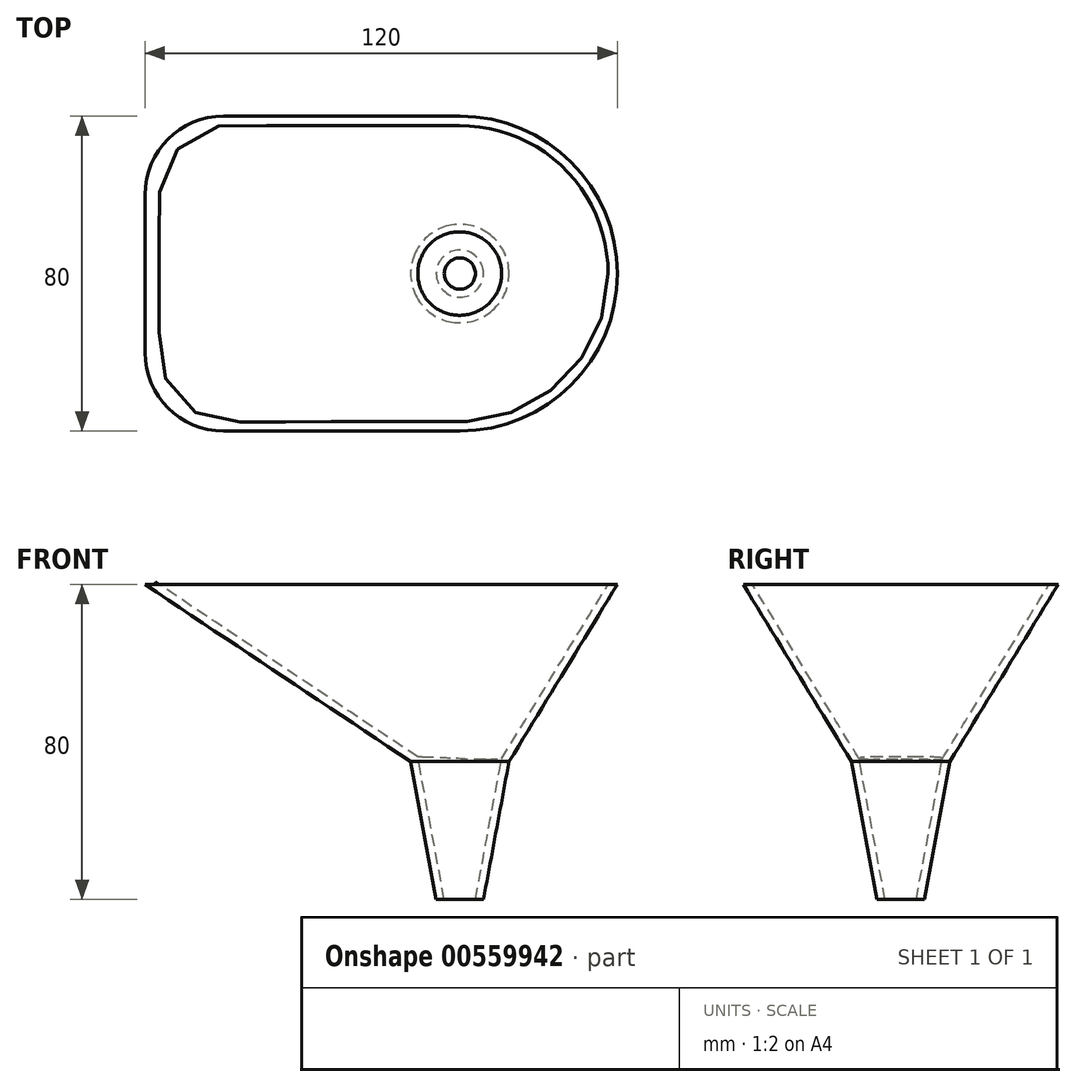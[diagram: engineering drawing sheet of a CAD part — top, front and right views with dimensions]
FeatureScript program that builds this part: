
annotation { "Feature Type Name" : "Feature", "Feature Type Description" : "" }
export const myFeature = defineFeature(function(context is Context, id is Id, definition is map)
    precondition{}
    {
        {
            var Q0;
            Q0=qCreatedBy(makeId("Top.planeOp"),FACE);
            var sketch = newSketch(context, id + "F0", { "sketchPlane" : qUnion([Q0])});
            skCircle(sketch, "E0", {"center": v(0, 0) * mm, "radius": 6 * mm});
            skSolve(sketch);
        }
        {
            var Q0;
            Q0=makeQuery(id+"F0.imprint","IMPRINT",FACE,{"disambiguationData":[TD([[makeQuery(id+"F0.imprint","IMPRINT",EDGE,{"derivedFrom":sQuery(id+"F0.wireOp",EDGE,"E0")}),1.0]])]});
            cPlane(context, id + "F1", {"entities" : qUnion([Q0]), "cplaneType" : CPlaneType.OFFSET, "offset" : 35 * mm, "width" : 150 * mm, "height" : 150 * mm});
        }
        {
            var Q0;
            Q0=qCreatedBy(id+"F1.planeOp",FACE);
            var sketch = newSketch(context, id + "F2", { "sketchPlane" : qUnion([Q0])});
            skCircle(sketch, "E1", {"center": v(0, 0) * mm, "radius": 12.5 * mm});
            skSolve(sketch);
        }
        {
            var Q0;
            Q0=makeQuery(id+"F0.imprint","IMPRINT",FACE,{"disambiguationData":[TD([[makeQuery(id+"F0.imprint","IMPRINT",EDGE,{"derivedFrom":sQuery(id+"F0.wireOp",EDGE,"E0")}),1.0]])]});
            var Q1;
            Q1=makeQuery(id+"F2.imprint","IMPRINT",FACE,{"disambiguationData":[TD([[makeQuery(id+"F2.imprint","IMPRINT",EDGE,{"derivedFrom":sQuery(id+"F2.wireOp",EDGE,"E1")}),1.0]])]});
            loft(context, id + "F3", {"sheetProfilesArray" : [{ "sheetProfileEntities" : qUnion([Q0]) }, { "sheetProfileEntities" : qUnion([Q1]) }]});
        }
        {
            var Q0;
            Q0=makeQuery(id+"F3.opLoft","CAP_FACE",FACE,{"disambiguationData":[OSD([makeQuery(id+"F2.imprint","IMPRINT",FACE,{"disambiguationData":[TD([[makeQuery(id+"F2.imprint","IMPRINT",EDGE,{"derivedFrom":sQuery(id+"F2.wireOp",EDGE,"E1")}),1.0]])]})])],"isStart":true});
            cPlane(context, id + "F4", {"entities" : qUnion([Q0]), "cplaneType" : CPlaneType.OFFSET, "offset" : 45 * mm, "width" : 150 * mm, "height" : 150 * mm});
        }
        {
            var Q0;
            Q0=qCreatedBy(id+"F4.planeOp",FACE);
            var sketch = newSketch(context, id + "F5", { "sketchPlane" : qUnion([Q0])});
            skArc(sketch, "E2", {"start": v(40, 0) * mm, "mid": v(28.28, 28.28) * mm, "end": v(0, 40) * mm});
            skArc(sketch, "E3", {"start": v(40, 0) * mm, "mid": v(28.28, -28.28) * mm, "end": v(0, -40) * mm});
            skLineSegment(sketch, "E4", {"start": v(0, 40) * mm, "end": v(-60, 40) * mm});
            skLineSegment(sketch, "E5", {"start": v(0, -40) * mm, "end": v(-60, -40) * mm});
            skLineSegment(sketch, "E6", {"start": v(-80, -20) * mm, "end": v(-80, 20) * mm});
            skPoint(sketch, "E7.visualSharp", {"position": v(-80, 40) * mm});
            skArc(sketch, "E7.filletArc", {"start": v(-60, 40) * mm, "mid": v(-74.14, 34.14) * mm, "end": v(-80, 20) * mm});
            skPoint(sketch, "E8.visualSharp", {"position": v(-80, -40) * mm});
            skArc(sketch, "E8.filletArc", {"start": v(-80, -20) * mm, "mid": v(-74.14, -34.14) * mm, "end": v(-60, -40) * mm});
            skSolve(sketch);
        }
        {
            var Q0;
            Q0=makeQuery(id+"F3.opLoft","CAP_FACE",FACE,{"disambiguationData":[OSD([makeQuery(id+"F2.imprint","IMPRINT",FACE,{"disambiguationData":[TD([[makeQuery(id+"F2.imprint","IMPRINT",EDGE,{"derivedFrom":sQuery(id+"F2.wireOp",EDGE,"E1")}),1.0]])]})])],"isStart":true});
            var Q1;
            Q1=makeQuery(id+"F5.imprint","IMPRINT",FACE,{"disambiguationData":[TD([[makeQuery(id+"F5.imprint","IMPRINT",EDGE,{"derivedFrom":sQuery(id+"F5.wireOp",EDGE,"E2")}),1.0]])]});
            loft(context, id + "F6", {"operationType" : NewBodyOperationType.ADD, "sheetProfilesArray" : [{ "sheetProfileEntities" : qUnion([Q0]) }, { "sheetProfileEntities" : qUnion([Q1]) }]});
        }
        {
            var Q0;
            Q0=makeQuery(id+"F6.opLoft","CAP_FACE",FACE,{"disambiguationData":[OSD([makeQuery(id+"F5.imprint","IMPRINT",FACE,{"disambiguationData":[TD([[makeQuery(id+"F5.imprint","IMPRINT",EDGE,{"derivedFrom":sQuery(id+"F5.wireOp",EDGE,"E2")}),1.0]])]})])],"isStart":true});
            var Q1;
            Q1=makeQuery(id+"F3.opLoft","CAP_FACE",FACE,{"disambiguationData":[OSD([makeQuery(id+"F0.imprint","IMPRINT",FACE,{"disambiguationData":[TD([[makeQuery(id+"F0.imprint","IMPRINT",EDGE,{"derivedFrom":sQuery(id+"F0.wireOp",EDGE,"E0")}),1.0]])]})])],"isStart":true});
            shell(context, id + "F7", {"entities" : qUnion([Q0, Q1]), "thickness" : 2 * mm});
        }
    });
